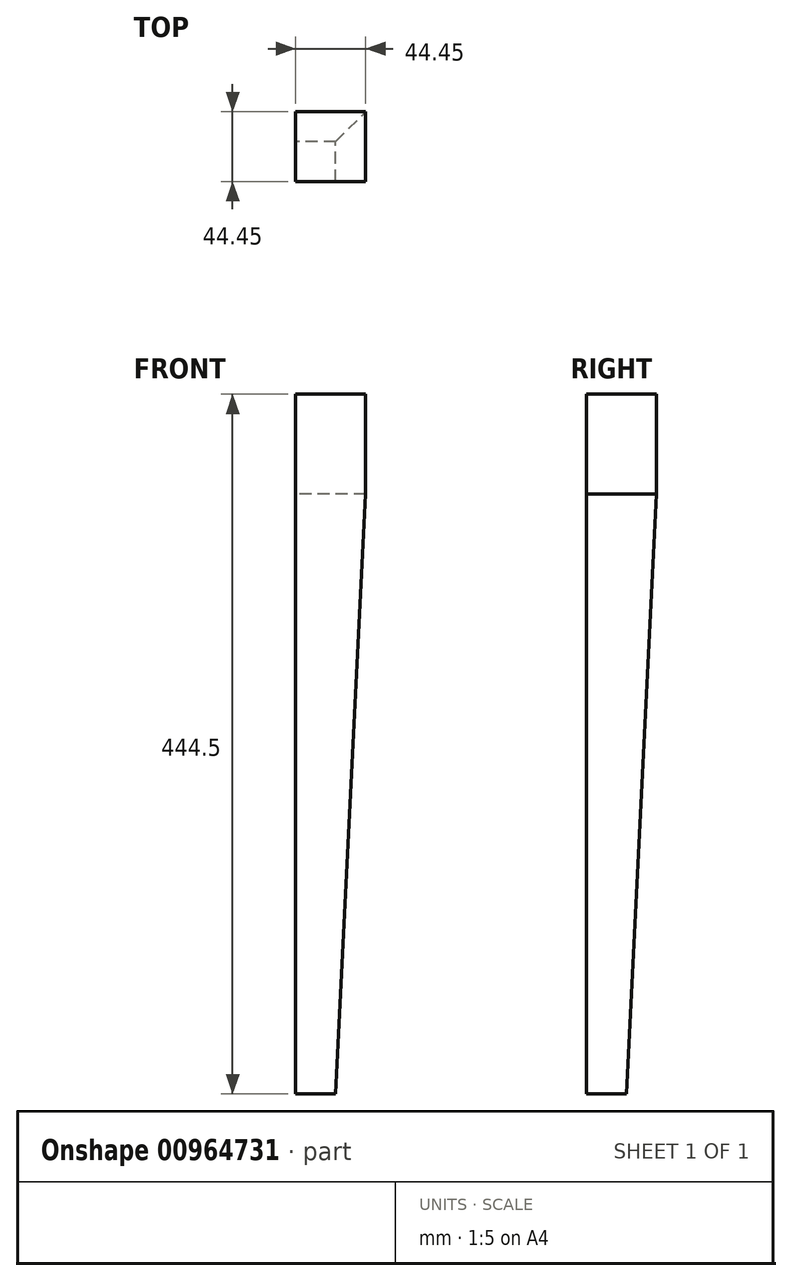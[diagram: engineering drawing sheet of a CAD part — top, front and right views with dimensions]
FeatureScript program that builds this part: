
annotation { "Feature Type Name" : "Feature", "Feature Type Description" : "" }
export const myFeature = defineFeature(function(context is Context, id is Id, definition is map)
    precondition{}
    {
        {
            var Q0;
            Q0=qCreatedBy(makeId("Front.planeOp"),FACE);
            var sketch = newSketch(context, id + "F0", { "sketchPlane" : qUnion([Q0])});
            skLineSegment(sketch, "E0", {"start": v(0, 0) * mm, "end": v(0, 444.5) * mm});
            skLineSegment(sketch, "E1", {"start": v(0, 444.5) * mm, "end": v(44.45, 444.5) * mm});
            skLineSegment(sketch, "E2", {"start": v(44.45, 444.5) * mm, "end": v(44.45, 381) * mm});
            skLineSegment(sketch, "E3", {"start": v(44.45, 381) * mm, "end": v(25.4, 0) * mm});
            skLineSegment(sketch, "E4", {"start": v(25.4, 0) * mm, "end": v(0, 0) * mm});
            skSolve(sketch);
        }
        {
            var Q0;
            Q0 = qSketchRegion(id + "F0", true);
            extrude(context, id + "F1", {"entities" : qUnion([Q0]), "depth" : 44.45 * mm, "offsetDistance" : 25.4 * mm});
        }
        {
            var Q0;
            Q0=makeQuery(id+"F1.opExtrude","SWEPT_FACE",FACE,{"disambiguationData":[OSD([sQuery(id+"F0.wireOp",EDGE,"E0")])]});
            var sketch = newSketch(context, id + "F2", { "sketchPlane" : qUnion([Q0])});
            skLineSegment(sketch, "E5", {"start": v(0, 0) * mm, "end": v(0, 381) * mm});
            skLineSegment(sketch, "E6", {"start": v(0, 381) * mm, "end": v(19.05, 0) * mm});
            skLineSegment(sketch, "E7", {"start": v(19.05, 0) * mm, "end": v(0, 0) * mm});
            skSolve(sketch);
        }
        {
            var Q0;
            Q0 = qSketchRegion(id + "F2", true);
            extrude(context, id + "F3", {"entities" : qUnion([Q0]), "operationType" : NewBodyOperationType.REMOVE, "endBound" : BoundingType.THROUGH_ALL, "oppositeDirection" : true, "depth" : 25.4 * mm, "offsetDistance" : 25.4 * mm});
        }
    });
